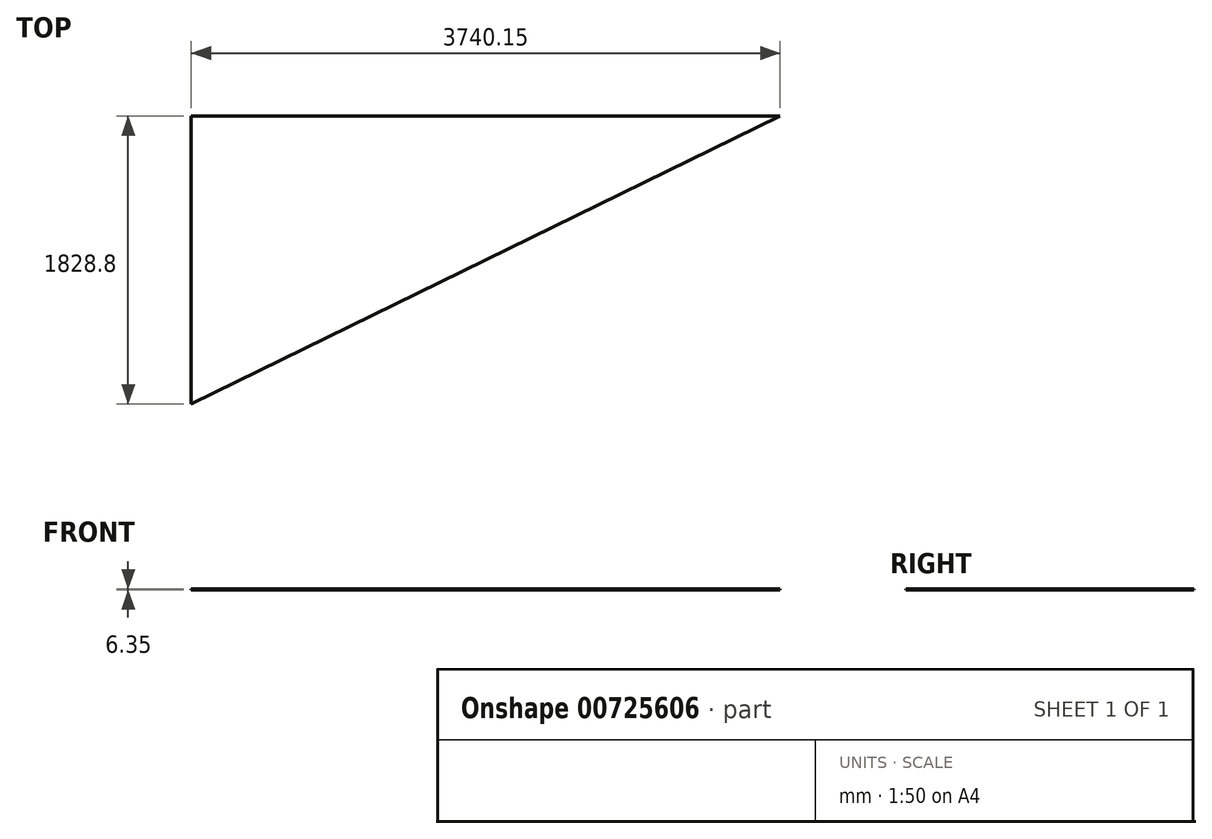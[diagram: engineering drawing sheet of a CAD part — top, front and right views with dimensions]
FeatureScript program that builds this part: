
annotation { "Feature Type Name" : "Feature", "Feature Type Description" : "" }
export const myFeature = defineFeature(function(context is Context, id is Id, definition is map)
    precondition{}
    {
        {
            var Q0;
            Q0=qCreatedBy(makeId("Top.planeOp"),FACE);
            var sketch = newSketch(context, id + "F0", { "sketchPlane" : qUnion([Q0])});
            skLineSegment(sketch, "E0", {"start": v(0, 0) * mm, "end": v(3740.15, 0) * mm});
            skLineSegment(sketch, "E1", {"start": v(3740.15, 0) * mm, "end": v(0, -1828.8) * mm});
            skLineSegment(sketch, "E2", {"start": v(0, -1828.8) * mm, "end": v(0, 0) * mm});
            skSolve(sketch);
        }
        {
            var Q0;
            Q0 = qSketchRegion(id + "F0", true);
            extrude(context, id + "F1", {"entities" : qUnion([Q0]), "depth" : 6.35 * mm, "offsetDistance" : 25.4 * mm});
        }
    });
